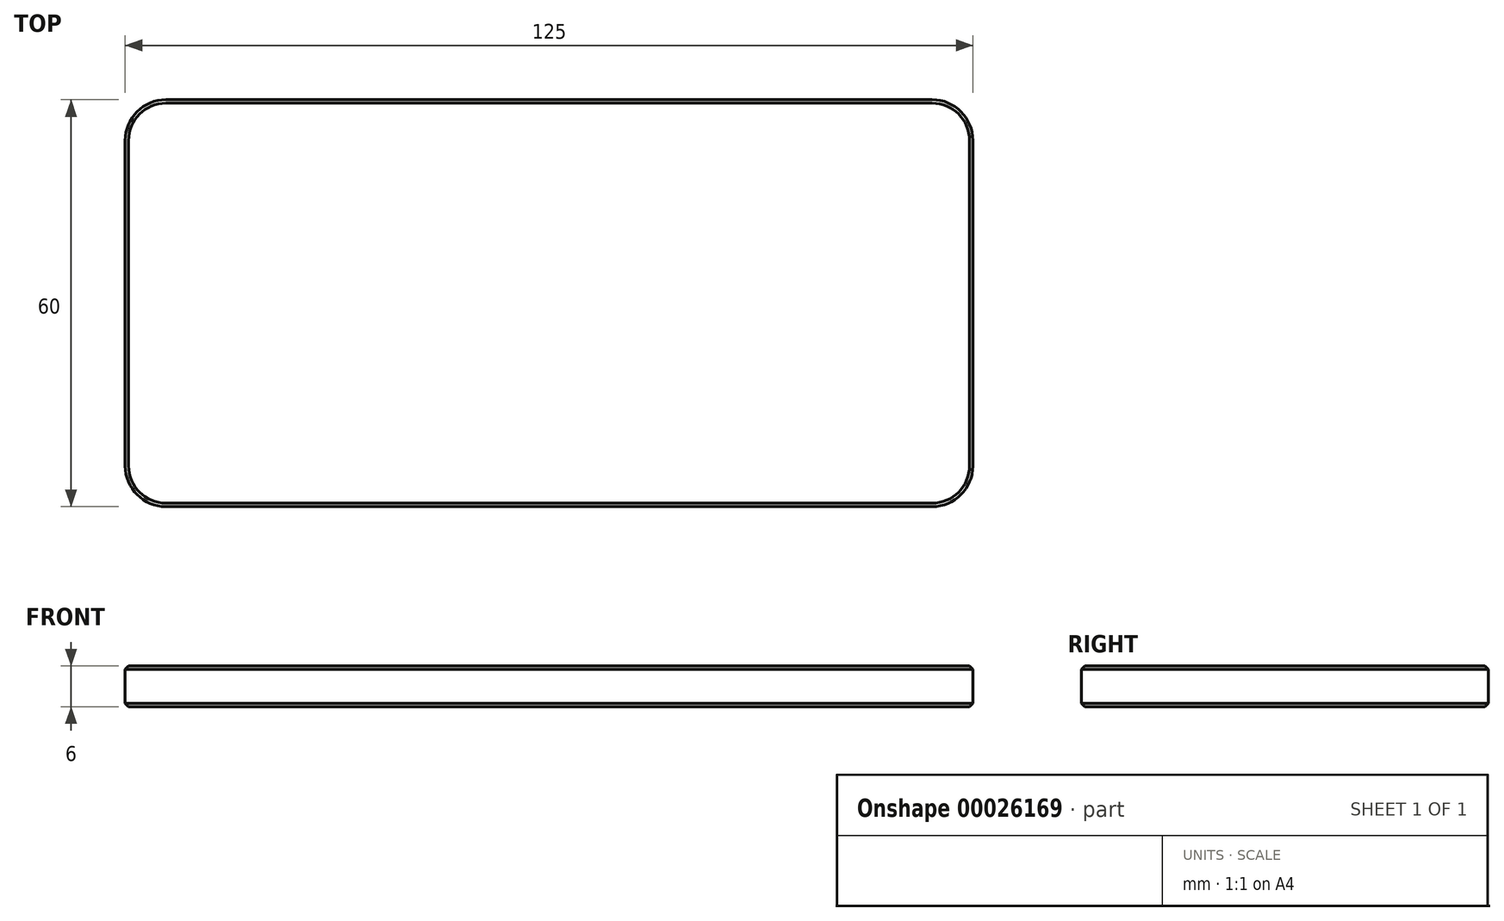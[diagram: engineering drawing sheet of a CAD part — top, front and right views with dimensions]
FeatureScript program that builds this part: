
annotation { "Feature Type Name" : "Feature", "Feature Type Description" : "" }
export const myFeature = defineFeature(function(context is Context, id is Id, definition is map)
    precondition{}
    {
        {
            var Q0;
            Q0=qCreatedBy(makeId("Top.planeOp"),FACE);
            var sketch = newSketch(context, id + "F0", { "sketchPlane" : qUnion([Q0])});
            skLineSegment(sketch, "E0.bottom", {"start": v(-60.83, 0) * mm, "end": v(64.17, 0) * mm});
            skLineSegment(sketch, "E0.top", {"start": v(-60.83, -60) * mm, "end": v(64.17, -60) * mm});
            skLineSegment(sketch, "E0.left", {"start": v(-60.83, 0) * mm, "end": v(-60.83, -60) * mm});
            skLineSegment(sketch, "E0.right", {"start": v(64.17, 0) * mm, "end": v(64.17, -60) * mm});
            skSolve(sketch);
        }
        {
            var Q0;
            Q0=makeQuery(id+"F0.imprint","IMPRINT",FACE,{"disambiguationData":[TD([[makeQuery(id+"F0.imprint","IMPRINT",EDGE,{"derivedFrom":sQuery(id+"F0.wireOp",EDGE,"E0.bottom")}),-1.0]])]});
            extrude(context, id + "F1", {"entities" : qUnion([Q0]), "depth" : 6 * mm});
        }
        {
            var Q0;
            Q0=makeQuery(id+"F1.opExtrude","SWEPT_EDGE",EDGE,{"disambiguationData":[OSD([sQuery(id+"F0.wireOp",EDGE,"E0.top"),sQuery(id+"F0.wireOp",EDGE,"E0.left")])]});
            var Q1;
            Q1=makeQuery(id+"F1.opExtrude","SWEPT_EDGE",EDGE,{"disambiguationData":[OSD([sQuery(id+"F0.wireOp",EDGE,"E0.top"),sQuery(id+"F0.wireOp",EDGE,"E0.right")])]});
            var Q2;
            Q2=makeQuery(id+"F1.opExtrude","SWEPT_EDGE",EDGE,{"disambiguationData":[OSD([sQuery(id+"F0.wireOp",EDGE,"E0.bottom"),sQuery(id+"F0.wireOp",EDGE,"E0.left")])]});
            var Q3;
            Q3=makeQuery(id+"F1.opExtrude","SWEPT_EDGE",EDGE,{"disambiguationData":[OSD([sQuery(id+"F0.wireOp",EDGE,"E0.bottom"),sQuery(id+"F0.wireOp",EDGE,"E0.right")])]});
            fillet(context, id + "F2", {"entities" : qUnion([Q0, Q1, Q2, Q3]), "radius" : 6 * mm, "tangentPropagation" : true, "allowEdgeOverflow" : false});
        }
        {
            var Q0;
            Q0=makeQuery(id+"F1.opExtrude","CAP_FACE",FACE,{"disambiguationData":[OSD([sQuery(id+"F0.wireOp",EDGE,"E0.bottom"),sQuery(id+"F0.wireOp",EDGE,"E0.top"),sQuery(id+"F0.wireOp",EDGE,"E0.left"),sQuery(id+"F0.wireOp",EDGE,"E0.right")])],"isStart":false});
            var Q1;
            Q1=makeQuery(id+"F1.opExtrude","CAP_FACE",FACE,{"disambiguationData":[OSD([sQuery(id+"F0.wireOp",EDGE,"E0.bottom"),sQuery(id+"F0.wireOp",EDGE,"E0.top"),sQuery(id+"F0.wireOp",EDGE,"E0.left"),sQuery(id+"F0.wireOp",EDGE,"E0.right")])],"isStart":true});
            chamfer(context, id + "F3", {"entities" : qUnion([Q0, Q1]), "width" : 0.5 * mm, "tangentPropagation" : true});
        }
    });
